# Revit family: Gelenkbogen-Element RGBEV 620FT
name_source: partatom
category: Generic Models
revit_build: Autodesk Revit 2017 (Build: 20190508_0315(x64)
units: mm (PartAtom-declared; Revit-internal decimal feet)

## family parameters
Always vertical = Yes
Can host rebar = No
Cut with Voids When Loaded = No
Part Type = Normal
Room Calculation Point = No
Round Connector Dimension = Use Diameter
Shared = No
Work Plane-Based = No

## types (1)
- RGBEV 620 FT
    Article Type = RGBEV 620 FT
    Cut's number = 2
    Cut's number 2 = 4
    GTIN = 4012196228133
    Length = 288 mm  [stored 0.944882 ft]
    Manufacturer = OBO BETTERMANN
    Manufacturer Art.No. = 7075200
    Material = Hot dip galvanised
    URL = http://www.obo-bettermann.com
    Width = 200 mm  [stored 0.656168 ft]
    Width 1 = 100 mm  [stored 0.328084 ft]

note: [stored X ft] marks values corroborated as IEEE doubles in the binary element streams (Revit-internal decimal feet)

## geometry (parser evidence)
native form markers: Sweep x2
no freeform markers — native parametric forms only
